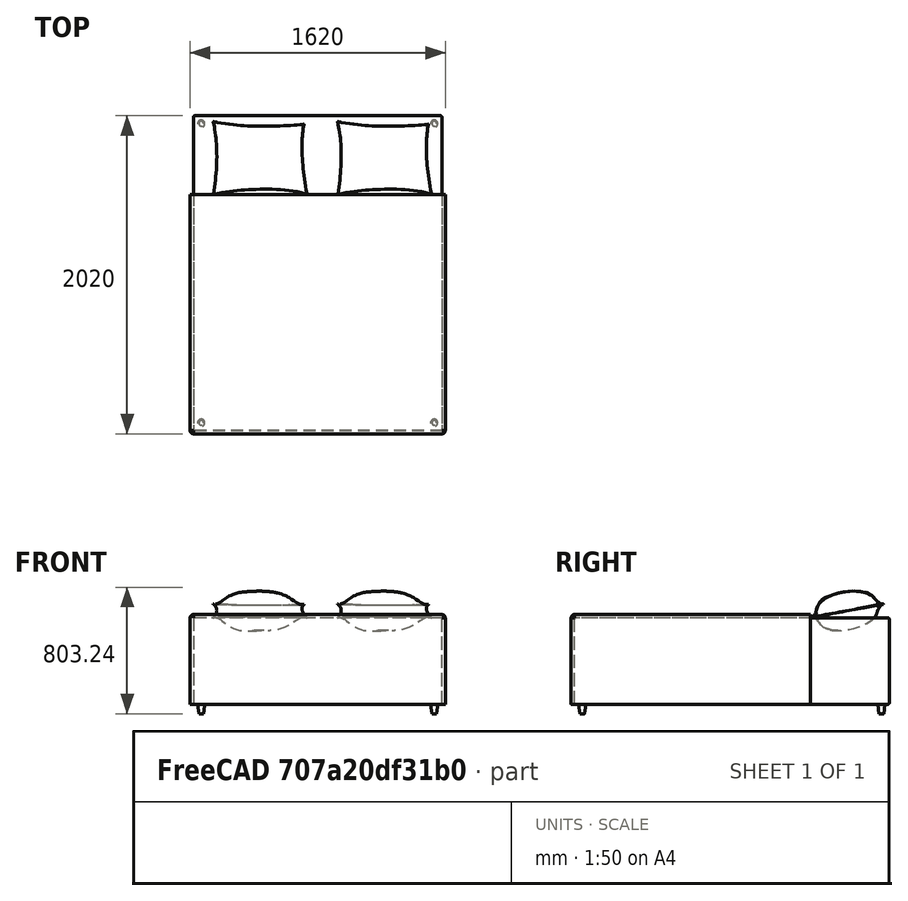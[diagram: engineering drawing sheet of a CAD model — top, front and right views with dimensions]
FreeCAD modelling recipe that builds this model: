
FCSTD DOCUMENT  (FreeCAD 0.21R33668 +26 (Git))
Label: Cama
License: All rights reserved
objects: Sketcher::SketchObject×6, Part::FeaturePython×5, Part::Extrusion×2, PartDesign::Body×2, PartDesign::Fillet×1, Part::Loft×1, PartDesign::Thickness×1, Part::Feature×1, Part::Compound×1
note: 22 computed .brp shape members not serialized (recipe doc carries the construction recipe); baked Part::Feature solids carry a one-line shape summary decoded from their .brp

FEATURE [Sketcher::SketchObject] Sketch
  FullyConstrained = true
  Placement = pos=(0,0,0) rot=(1,0,0;1.5708rad)
  expr: Constraints[10] = <<Propriedades cama>>.Altura - <<Propriedades cama>>.AlturaPe
  expr: Constraints[9] = <<Propriedades cama>>.Largura
  sketch-geometry (4):
    g0: LineSegment StartX=0 StartY=0 StartZ=0 EndX=1580 EndY=0 EndZ=0
    g1: LineSegment StartX=1580 StartY=0 StartZ=0 EndX=1580 EndY=550 EndZ=0
    g2: LineSegment StartX=1580 StartY=550 StartZ=0 EndX=0 EndY=550 EndZ=0
    g3: LineSegment StartX=0 StartY=550 StartZ=0 EndX=0 EndY=0 EndZ=0
  constraints (11):
    c: Coincident(g0,g1)
    c: Coincident(g1,g2)
    c: Coincident(g2,g3)
    c: Coincident(g3,g0)
    c: Horizontal(g0)
    c: Horizontal(g2)
    c: Vertical(g1)
    c: Vertical(g3)
    c: Coincident(g0,g-1)
    c: DistanceX(g2,g2) = 1580
    c: DistanceY(g1,g1) = 550
FEATURE [Part::FeaturePython] Point  label="Propriedades cama"  # WARN: FeaturePython — macro-defined, semantics opaque (R4)
  Altura = 610
  AlturaPe = 60
  Comprimento = 2000
  Largura = 1580
  LarguraPe = 30
  NumAlmofadas = 2
  X = 0
  Y = 0
  Z = 0
FEATURE [Part::Extrusion] Extrude
  Base = -> Sketch
  Dir = (0,-1,2e-16)
  DirMode = 2
  FaceMakerClass = Part::FaceMakerBullseye
  LengthFwd = 0
  LengthRev = 2000
  Solid = true
  Symmetric = false
  expr: LengthRev = <<Propriedades cama>>.Comprimento
FEATURE [PartDesign::Fillet] Fillet
  Base = -> Extrude [Face3,Face4,Face6,Face2,Face5,Face1]
  Radius = 10
  SupportTransform = false
  UseAllEdges = false
FEATURE [PartDesign::Body] Body  label="Cama"
  Group = -> [Extrude,Fillet]
  Origin = -> Origin
  Placement = pos=(0,0,60) rot=(0,0,1;0rad)
  Tip = -> Fillet
  expr: .Placement.Base.z = <<Propriedades cama>>.AlturaPe
FEATURE [Sketcher::SketchObject] Sketch001
  FullyConstrained = true
  expr: Constraints[1] = <<Propriedades cama>>.LarguraPe
  sketch-geometry (1):
    g0: Circle CenterX=0 CenterY=0 CenterZ=0 NormalX=0 NormalY=0 NormalZ=1 AngleXU=0 Radius=15
  constraints (2):
    c: Coincident(g0,g-1)
    c: Diameter(g0) = 30
FEATURE [Sketcher::SketchObject] Sketch002
  FullyConstrained = true
  Placement = pos=(0,0,60) rot=(0,0,1;0rad)
  expr: .Placement.Base.z = <<Propriedades cama>>.AlturaPe
  expr: Constraints[1] = 1.5 * <<Propriedades cama>>.LarguraPe
  sketch-geometry (1):
    g0: Circle CenterX=0 CenterY=0 CenterZ=0 NormalX=0 NormalY=0 NormalZ=1 AngleXU=0 Radius=22.5
  constraints (2):
    c: Coincident(g0,g-1)
    c: Diameter(g0) = 45
FEATURE [Part::Loft] Loft  label="Pé"
  Closed = false
  MaxDegree = 5
  Placement = pos=(50,50,0) rot=(0,0,1;0rad)
  Ruled = false
  Sections = -> [Sketch002,Sketch001]
  Solid = true
FEATURE [Part::FeaturePython] Clone  label="Pé001"  # Draft clone (typed FeaturePython)
  AttacherType = Attacher::AttachEngine3D
  Fuse = false
  Objects = -> [Loft]
  Placement = pos=(1530,50,0) rot=(0,0,1;0rad)
  Scale = (1,1,1)
  expr: .Placement.Base.x = <<Propriedades cama>>.Largura - 5 cm
FEATURE [Part::FeaturePython] Clone001  label="Pé002"  # Draft clone (typed FeaturePython)
  AttacherType = Attacher::AttachEngine3D
  Fuse = false
  Objects = -> [Loft]
  Placement = pos=(50,1950,0) rot=(0,0,1;0rad)
  Scale = (1,1,1)
  expr: .Placement.Base.y = <<Propriedades cama>>.Comprimento - 5 cm
FEATURE [Part::FeaturePython] Clone002  label="Pé003"  # Draft clone (typed FeaturePython)
  AttacherType = Attacher::AttachEngine3D
  Fuse = false
  Objects = -> [Loft]
  Placement = pos=(1530,1950,0) rot=(0,0,1;0rad)
  Scale = (1,1,1)
  expr: .Placement.Base.x = <<Propriedades cama>>.Largura - 5 cm
  expr: .Placement.Base.y = <<Propriedades cama>>.Comprimento - 5 cm
FEATURE [Sketcher::SketchObject] Sketch003
  FullyConstrained = false
  sketch-geometry (32):
    g0-g4: Circle x5 (B-spline internal-alignment scaffolding for g5; pole/knot coordinates omitted)
    g5: BSplineCurve PolesCount=5 KnotsCount=3 Degree=3 IsPeriodic=0
    g6: GeomPoint X=0 Y=0 Z=0
    g7: GeomPoint X=364.031 Y=44.1226 Z=0
    g8: GeomPoint X=744.605 Y=0 Z=0
    g9-g13: Circle x5 (B-spline internal-alignment scaffolding for g14; pole/knot coordinates omitted)
    g14: BSplineCurve PolesCount=5 KnotsCount=3 Degree=3 IsPeriodic=0
    g15: GeomPoint X=0 Y=587.937 Z=0
    g16: GeomPoint X=378.099 Y=549.307 Z=0
    g17: GeomPoint X=720.123 Y=566.986 Z=0
    g18-g21: Circle x4 (B-spline internal-alignment scaffolding for g22; pole/knot coordinates omitted)
    g22: BSplineCurve PolesCount=4 KnotsCount=2 Degree=3 IsPeriodic=0
    g23: GeomPoint X=0 Y=587.937 Z=0
    g24: GeomPoint X=0 Y=0 Z=0
    g25-g28: Circle x4 (B-spline internal-alignment scaffolding for g29; pole/knot coordinates omitted)
    g29: BSplineCurve PolesCount=4 KnotsCount=2 Degree=3 IsPeriodic=0
    g30: GeomPoint X=720.123 Y=566.986 Z=0
    g31: GeomPoint X=744.605 Y=0 Z=0
  constraints (33):
    c: Weight(g0) = 1
    c: Coincident(g5,g-1)
    c: Equal(g0, g1-g4) x4
    c: PointOnObject(g5,g-1)
    c: InternalAlignment(g0-g4 -> g5) x5
    c: InternalAlignment(g6,g5)
    c: InternalAlignment(g7,g5)
    c: InternalAlignment(g8,g5)
    c: Weight(g9) = 1
    c: PointOnObject(g14,g-2)
    c: Equal(g9, g10-g13) x4
    c: InternalAlignment(g9-g13 -> g14) x5
    c: InternalAlignment(g15,g14)
    c: InternalAlignment(g16,g14)
    c: InternalAlignment(g17,g14)
    c: Weight(g18) = 1
    c: Coincident(g22,g14)
    c: Equal(g18,g19)
    c: Equal(g18,g20)
    c: Equal(g18,g21)
    c: Coincident(g22,g5)
    c: InternalAlignment(g18-g21 -> g22) x4
    c: InternalAlignment(g23,g22)
    c: InternalAlignment(g24,g22)
    c: Weight(g25) = 1
    c: Coincident(g29,g14)
    c: Equal(g25,g26)
    c: Equal(g25,g27)
    c: Equal(g25,g28)
    c: Coincident(g29,g5)
    c: InternalAlignment(g25-g28 -> g29) x4
    c: InternalAlignment(g30,g29)
    c: InternalAlignment(g31,g29)
FEATURE [Sketcher::SketchObject] Sketch004
  FullyConstrained = false
  Placement = pos=(0,343.53,0) rot=(1,0,0;1.5708rad)
  sketch-geometry (7):
    g0-g3: Circle x4 (B-spline internal-alignment scaffolding for g4; pole/knot coordinates omitted)
    g4: BSplineCurve PolesCount=4 KnotsCount=2 Degree=3 IsPeriodic=0
    g5: GeomPoint X=104.891 Y=69.4941 Z=0
    g6: GeomPoint X=615.748 Y=67.5224 Z=0
  constraints (7):
    c: Weight(g0) = 1
    c: Equal(g0,g1)
    c: Equal(g0,g2)
    c: Equal(g0,g3)
    c: InternalAlignment(g0-g3 -> g4) x4
    c: InternalAlignment(g5,g4)
    c: InternalAlignment(g6,g4)
FEATURE [Sketcher::SketchObject] Sketch005
  FullyConstrained = false
  Placement = pos=(357.948,2.8e-14,0) rot=(0.57735,0.57735,0.57735;2.0944rad)
  sketch-geometry (7):
    g0-g3: Circle x4 (B-spline internal-alignment scaffolding for g4; pole/knot coordinates omitted)
    g4: BSplineCurve PolesCount=4 KnotsCount=2 Degree=3 IsPeriodic=0
    g5: GeomPoint X=70.4144 Y=56.8262 Z=0
    g6: GeomPoint X=518.546 Y=56.1115 Z=0
  constraints (7):
    c: Weight(g0) = 1
    c: Equal(g0,g1)
    c: Equal(g0,g2)
    c: Equal(g0,g3)
    c: InternalAlignment(g0-g3 -> g4) x4
    c: InternalAlignment(g5,g4)
    c: InternalAlignment(g6,g4)
FEATURE [Part::Extrusion] Extrude001
  Base = -> Sketch
  Dir = (0,-1,2e-16)
  DirMode = 2
  FaceMakerClass = Part::FaceMakerBullseye
  LengthFwd = 0
  LengthRev = 1500
  Placement = pos=(0,0,60) rot=(0,0,1;0rad)
  Solid = true
  Symmetric = false
  expr: .Placement.Base.z = <<Propriedades cama>>.AlturaPe
  expr: LengthRev = <<Propriedades cama>>.Comprimento - 50 cm
FEATURE [PartDesign::Thickness] Thickness
  Base = -> Extrude001 [Face1,Face5]
  Intersection = false
  Join = 0
  Mode = 0
  SupportTransform = false
  Value = 20
FEATURE [PartDesign::Body] Body001  label="Roupa de cama"
  Group = -> [Extrude001,Thickness]
  Origin = -> Origin001
  Tip = -> Thickness
FEATURE [Part::Feature] Clone004  label="Almofada"
  Placement = pos=(0,0,0) rot=(-1,0,0;1.38732rad)
  shape: bbox 1588 x 23640 x 1929 mm, 16 faces, 2 solids (baked)
FEATURE [Part::FeaturePython] Array  # Draft array (typed FeaturePython)
  Angle = 360
  ArrayType = 0
  Axis = (0,0,1)
  Base = -> Clone004
  Center = (0,0,0)
  Count = 2
  Fuse = false
  IntervalAxis = (0,0,0)
  IntervalX = (790,0,0)
  IntervalY = (0,100,0)
  IntervalZ = (0,0,100)
  NumberCircles = 3
  NumberPolar = 5
  NumberX = 2
  NumberY = 1
  NumberZ = 1
  Placement = pos=(126.667,1500,610) rot=(0,0,1;0rad)
  RadialDistance = 50
  Symmetry = 1
  TangentialDistance = 25
  expr: .IntervalX.x = <<Propriedades cama>>.Largura / <<Propriedades cama>>.NumAlmofadas
  expr: .Placement.Base.x = <<Propriedades cama>>.Largura / (<<Propriedades cama>>.NumAlmofadas + 1) - 30 cm - (<<Propriedades cama>>.NumAlmofadas - 1) * 10 cm
  expr: .Placement.Base.y = <<Propriedades cama>>.Comprimento - 50 cm
  expr: .Placement.Base.z = <<Propriedades cama>>.Altura
  expr: NumberX = <<Propriedades cama>>.NumAlmofadas
FEATURE [Part::Compound] Compound  label="Cama "
  Links = -> [Array,Body,Loft,Clone,Clone001,Clone002,Sketch003,Sketch004,Sketch005,Body001]
